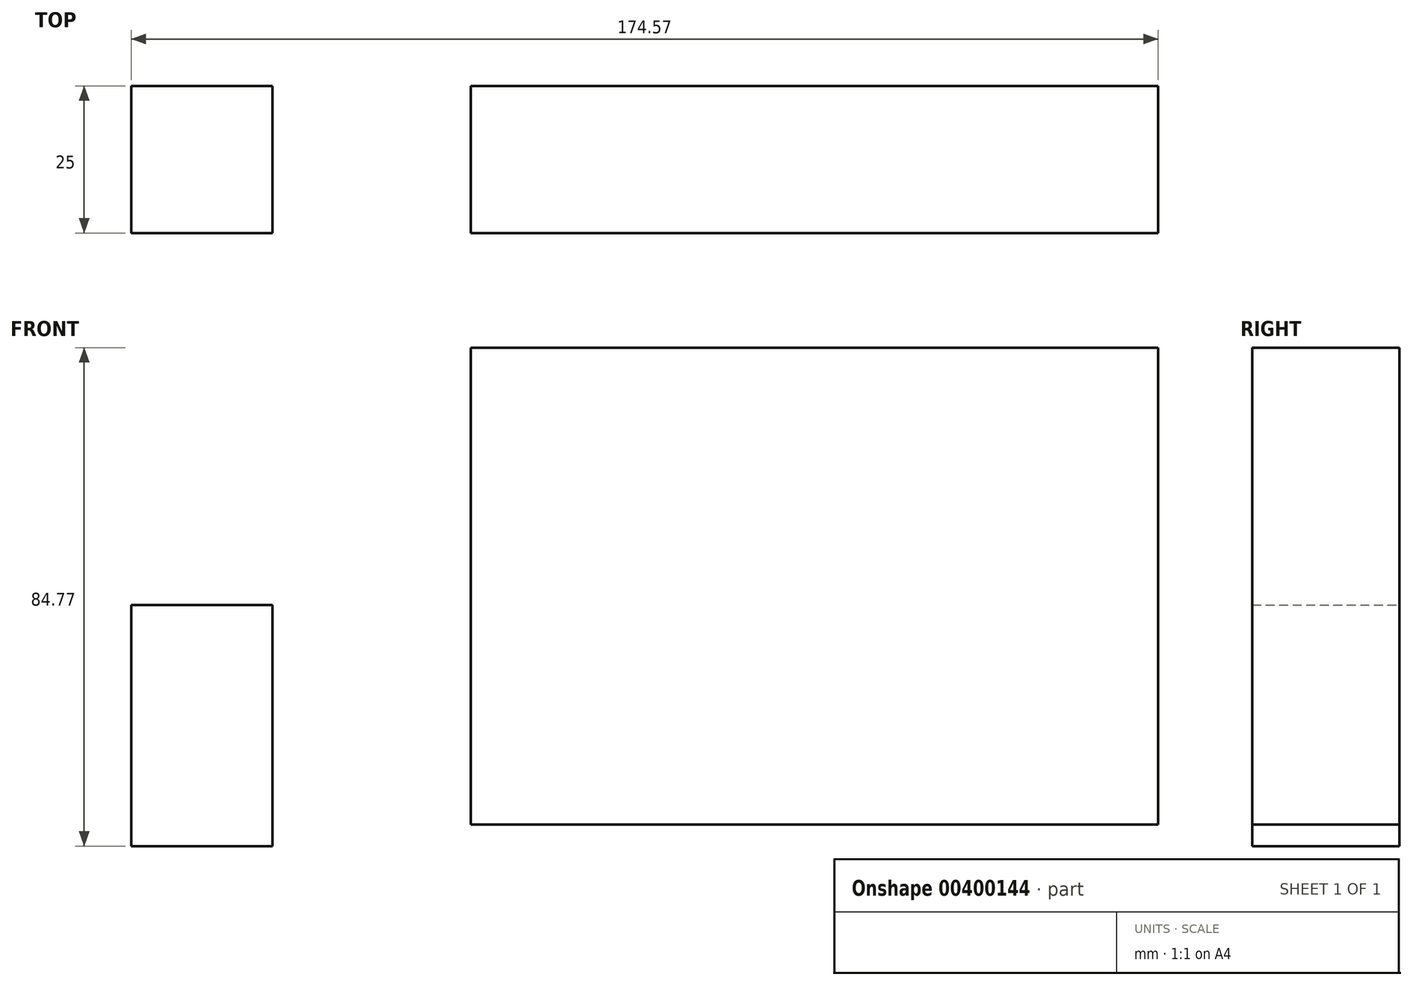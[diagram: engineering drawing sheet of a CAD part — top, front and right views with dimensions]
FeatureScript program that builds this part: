
annotation { "Feature Type Name" : "Feature", "Feature Type Description" : "" }
export const myFeature = defineFeature(function(context is Context, id is Id, definition is map)
    precondition{}
    {
        {
            var Q0;
            Q0=qCreatedBy(makeId("Front.planeOp"),FACE);
            var sketch = newSketch(context, id + "F0", { "sketchPlane" : qUnion([Q0])});
            skLineSegment(sketch, "E0.bottom", {"start": v(-76.44, 40.69) * mm, "end": v(-52.4, 40.69) * mm});
            skLineSegment(sketch, "E0.top", {"start": v(-76.44, 81.67) * mm, "end": v(-52.4, 81.67) * mm});
            skLineSegment(sketch, "E0.left", {"start": v(-76.44, 40.69) * mm, "end": v(-76.44, 81.67) * mm});
            skLineSegment(sketch, "E0.right", {"start": v(-52.4, 40.69) * mm, "end": v(-52.4, 81.67) * mm});
            skPoint(sketch, "E0.middle", {"position": v(-64.42, 61.18) * mm});
            skLineSegment(sketch, "E1.bottom", {"start": v(-18.7, 44.34) * mm, "end": v(98.13, 44.34) * mm});
            skLineSegment(sketch, "E1.top", {"start": v(-18.7, 125.46) * mm, "end": v(98.13, 125.46) * mm});
            skLineSegment(sketch, "E1.left", {"start": v(-18.7, 44.34) * mm, "end": v(-18.7, 125.46) * mm});
            skLineSegment(sketch, "E1.right", {"start": v(98.13, 44.34) * mm, "end": v(98.13, 125.46) * mm});
            skPoint(sketch, "E1.middle", {"position": v(39.72, 84.9) * mm});
            skSolve(sketch);
        }
        {
            var Q0;
            Q0 = qSketchRegion(id + "F0", true);
            extrude(context, id + "F1", {"entities" : qUnion([Q0]), "depth" : 25 * mm});
        }
    });
